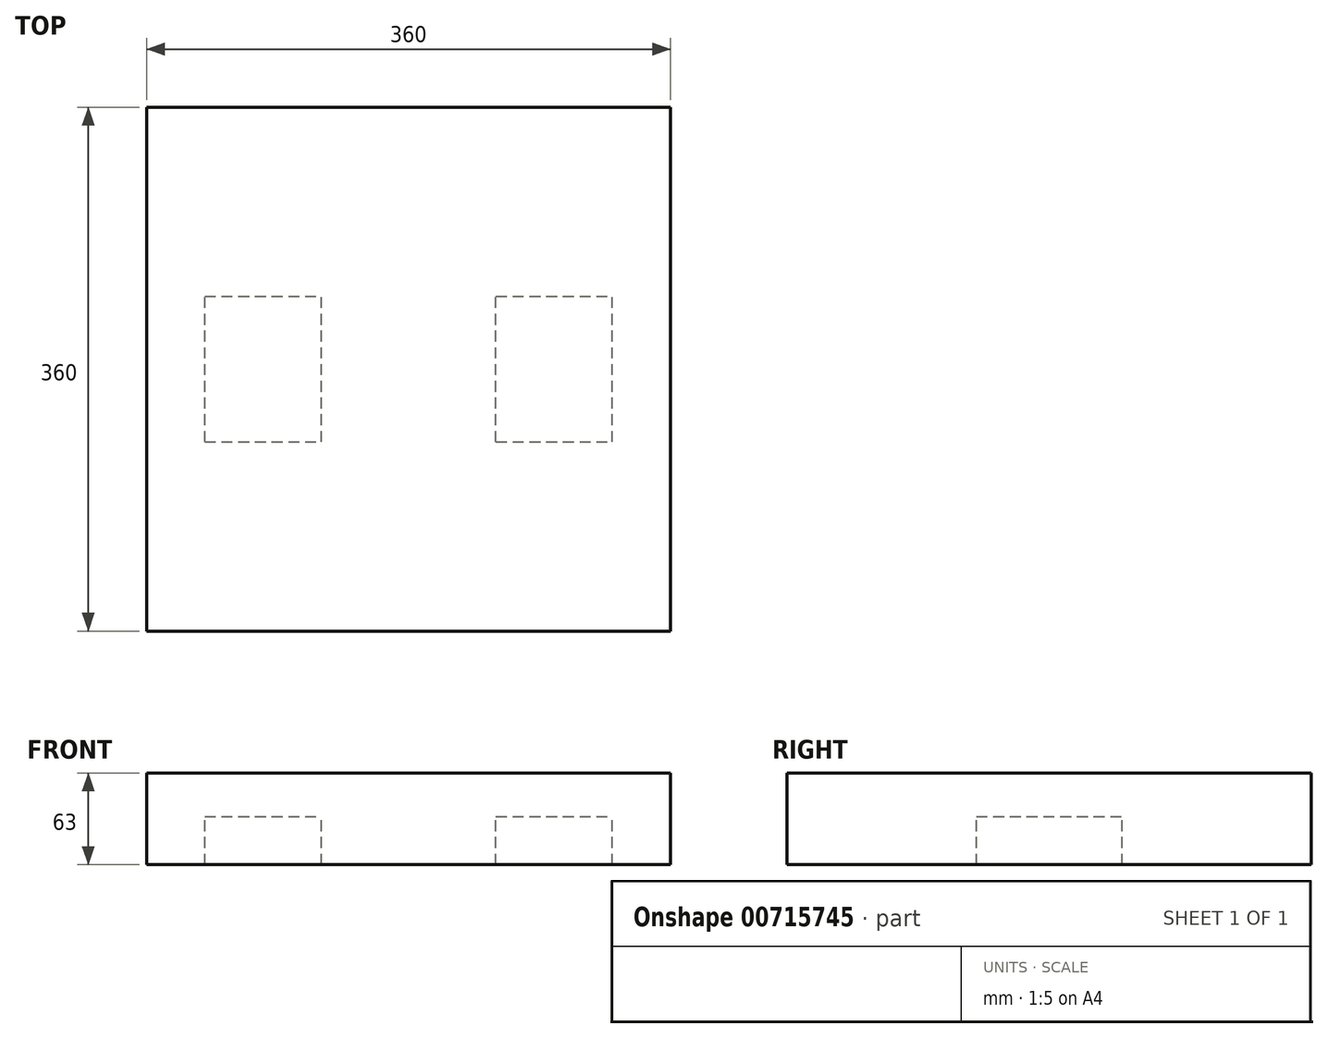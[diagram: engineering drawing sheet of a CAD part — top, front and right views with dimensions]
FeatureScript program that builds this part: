
annotation { "Feature Type Name" : "Feature", "Feature Type Description" : "" }
export const myFeature = defineFeature(function(context is Context, id is Id, definition is map)
    precondition{}
    {
        {
            var Q0;
            Q0=qCreatedBy(makeId("Top.planeOp"),FACE);
            var sketch = newSketch(context, id + "F0", { "sketchPlane" : qUnion([Q0])});
            skLineSegment(sketch, "E0.bottom", {"start": v(-180, 180) * mm, "end": v(180, 180) * mm});
            skLineSegment(sketch, "E0.top", {"start": v(-180, -180) * mm, "end": v(180, -180) * mm});
            skLineSegment(sketch, "E0.left", {"start": v(-180, 180) * mm, "end": v(-180, -180) * mm});
            skLineSegment(sketch, "E0.right", {"start": v(180, 180) * mm, "end": v(180, -180) * mm});
            skSolve(sketch);
        }
        {
            var Q0;
            Q0=qSketchRegion(id+"F0",true);
            extrude(context, id + "F1", {"entities" : qUnion([Q0]), "depth" : 30 * mm, "offsetDistance" : 25 * mm});
        }
        {
            var Q0;
            Q0=makeQuery(id+"F1.opExtrude","CAP_FACE",FACE,{"disambiguationData":[OSD([sQuery(id+"F0.wireOp",EDGE,"E0.bottom"),sQuery(id+"F0.wireOp",EDGE,"E0.top"),sQuery(id+"F0.wireOp",EDGE,"E0.left"),sQuery(id+"F0.wireOp",EDGE,"E0.right"),sQuery(id+"F0.wireOp",EDGE,"TyQa0Ud1-jUWR-pDTX-Flgi-0ZVLOhMCj8bS.bottom"),sQuery(id+"F0.wireOp",EDGE,"TyQa0Ud1-jUWR-pDTX-Flgi-0ZVLOhMCj8bS.top"),sQuery(id+"F0.wireOp",EDGE,"TyQa0Ud1-jUWR-pDTX-Flgi-0ZVLOhMCj8bS.left"),sQuery(id+"F0.wireOp",EDGE,"TyQa0Ud1-jUWR-pDTX-Flgi-0ZVLOhMCj8bS.right"),sQuery(id+"F0.wireOp",EDGE,"9HZlrwG0-1yuF-X62E-uwgh-WtHAEnwKVC0O.bottom"),sQuery(id+"F0.wireOp",EDGE,"9HZlrwG0-1yuF-X62E-uwgh-WtHAEnwKVC0O.top"),sQuery(id+"F0.wireOp",EDGE,"9HZlrwG0-1yuF-X62E-uwgh-WtHAEnwKVC0O.left"),sQuery(id+"F0.wireOp",EDGE,"9HZlrwG0-1yuF-X62E-uwgh-WtHAEnwKVC0O.right")])],"isStart":true});
            var sketch = newSketch(context, id + "F2", { "sketchPlane" : qUnion([Q0])});
            skLineSegment(sketch, "E1.bottom", {"start": v(-180, 180) * mm, "end": v(180, 180) * mm});
            skLineSegment(sketch, "E1.top", {"start": v(-180, -180) * mm, "end": v(180, -180) * mm});
            skLineSegment(sketch, "E1.left", {"start": v(-180, 180) * mm, "end": v(-180, -180) * mm});
            skLineSegment(sketch, "E1.right", {"start": v(180, 180) * mm, "end": v(180, -180) * mm});
            skLineSegment(sketch, "E2.bottom", {"start": v(-140, 50) * mm, "end": v(-60, 50) * mm});
            skLineSegment(sketch, "E2.top", {"start": v(-140, -50) * mm, "end": v(-60, -50) * mm});
            skLineSegment(sketch, "E2.left", {"start": v(-140, 50) * mm, "end": v(-140, -50) * mm});
            skLineSegment(sketch, "E2.right", {"start": v(-60, 50) * mm, "end": v(-60, -50) * mm});
            skLineSegment(sketch, "E3.bottom", {"start": v(60, 50) * mm, "end": v(140, 50) * mm});
            skLineSegment(sketch, "E3.top", {"start": v(60, -50) * mm, "end": v(140, -50) * mm});
            skLineSegment(sketch, "E3.left", {"start": v(60, 50) * mm, "end": v(60, -50) * mm});
            skLineSegment(sketch, "E3.right", {"start": v(140, 50) * mm, "end": v(140, -50) * mm});
            skSolve(sketch);
        }
        {
            var Q0;
            Q0 = qSketchRegion(id + "F2", true);
            extrude(context, id + "F3", {"entities" : qUnion([Q0]), "operationType" : NewBodyOperationType.ADD, "depth" : 33 * mm, "offsetDistance" : 25 * mm});
        }
    });
